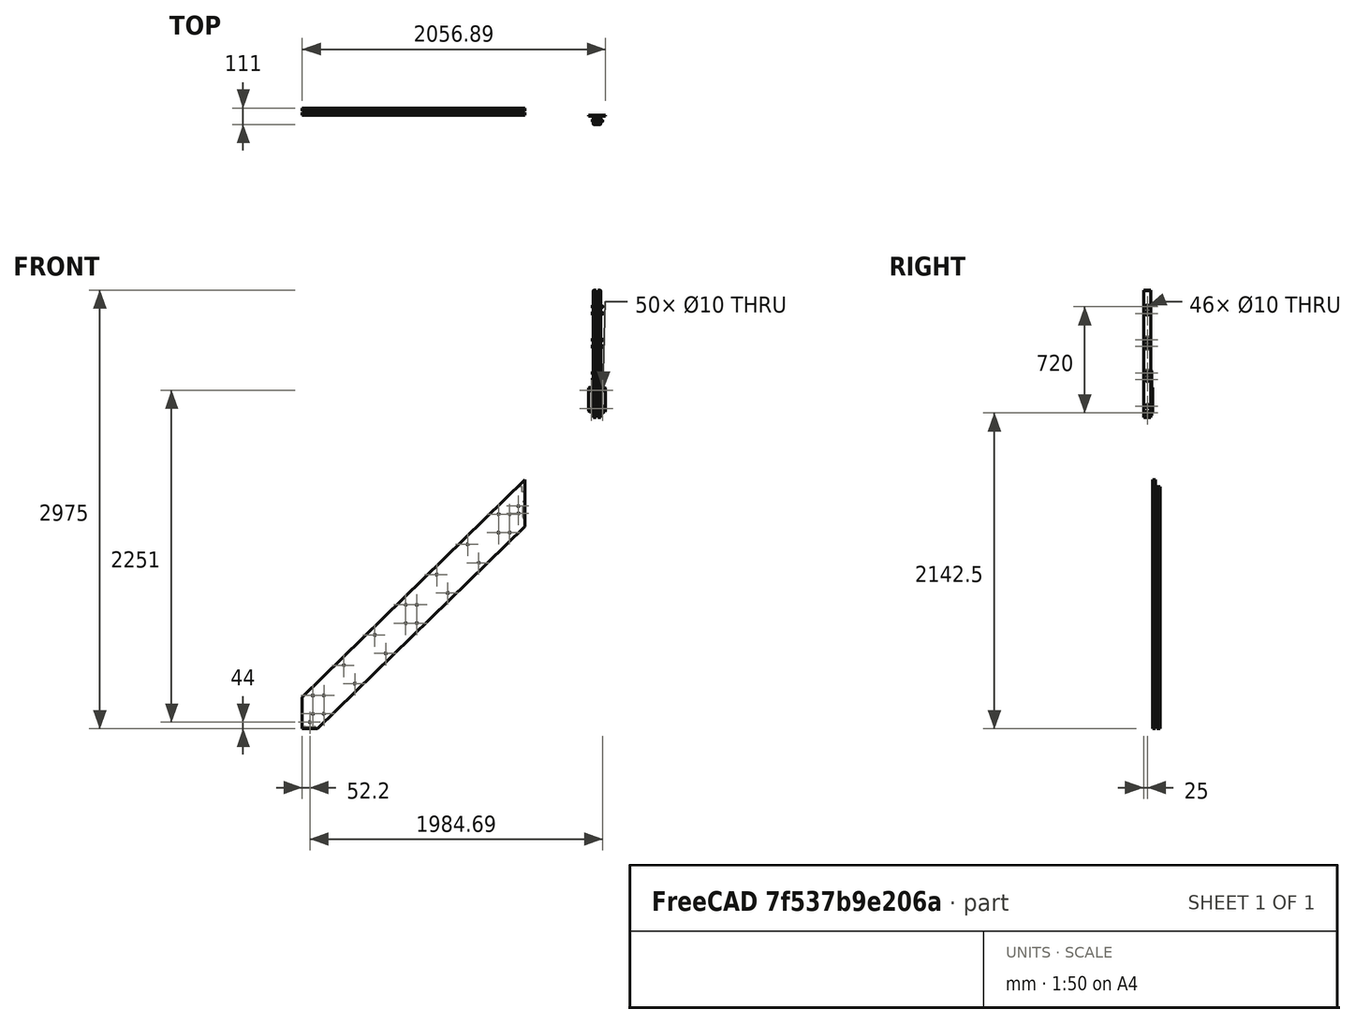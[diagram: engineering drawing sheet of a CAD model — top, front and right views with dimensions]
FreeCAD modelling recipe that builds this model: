
FCSTD DOCUMENT  (FreeCAD 0.17R10993 (Git))
Label: railing_last_wood
License: All rights reserved
LicenseURL: http://en.wikipedia.org/wiki/All_rights_reserved
objects: Part::Part2DObjectPython×22, Part::Feature×5, Part::FeaturePython×3, TechDraw::DrawProjGroupItem×3, App::DocumentObjectGroup×2, Part::Box×1, Part::Mirroring×1, Part::Compound×1, Part::Chamfer×1, Part::Extrusion×1, Part::Cut×1, TechDraw::DrawSVGTemplate×1, TechDraw::DrawProjGroup×1, TechDraw::DrawPage×1
note: 36 computed .brp shape members not serialized (recipe doc carries the construction recipe); baked Part::Feature solids carry a one-line shape summary decoded from their .brp

FEATURE [Part::Box] Box  label="Cube"
  AttacherType = Attacher::AttachEngine3D
  Height = 865
  Length = 20
  Placement = pos=(-25,-23,165) rot=(0,0,1;0rad)
  Width = 50
FEATURE [Part::Mirroring] mirror  label="Mirror of Cube"
  Base = (0,0,0)
  Normal = (1,0,0)
  Source = -> Box
FEATURE [Part::Compound] Compound
  Links = -> [mirror,Box]
  Placement = pos=(89.3902,-413,100) rot=(0,0,1;0rad)
FEATURE [Part::Chamfer] Chamfer  label="railing_wood"
  Base = -> Compound
  Edges = 24 edges r=2: [Edge1,Edge2,Edge3,Edge4,Edge5,Edge6,Edge7,Edge8,Edge9,Edge10,Edge11,Edge12,Edge13,Edge14,Edge15,Edge16,Edge17,Edge18,Edge19,Edge20,Edge21,Edge22,Edge23,Edge24]
FEATURE [Part::Feature] step_01_cs
  shape: bbox 1490 x 3e-07 x 1265 mm, 0 faces, 0 solids (baked)
FEATURE [Part::Feature] fridge_box_panels_01_cs
  shape: bbox 630 x 3e-07 x 2050 mm, 0 faces, 0 solids (baked)
FEATURE [Part::Part2DObjectPython] Line  # Draft 2D object (typed FeaturePython)
  ChamferSize = 0
  Closed = false
  End = (2100,-5,0)
  FilletRadius = 0
  Length = 2100.01
  MakeFace = true
  Points = (2) [(0,0,0),(2100,-5,0)]
  Start = (0,0,0)
  Subdivisions = 0
FEATURE [Part::Part2DObjectPython] Line002  # Draft 2D object (typed FeaturePython)
  ChamferSize = 0
  Closed = false
  End = (2900,0,2260)
  FilletRadius = 0
  Length = 800
  MakeFace = true
  Points = (2) [(2100,0,2260),(2900,0,2260)]
  Start = (2100,0,2260)
  Subdivisions = 0
FEATURE [Part::Part2DObjectPython] DWire  # Draft 2D object (typed FeaturePython)
  ChamferSize = 0
  Closed = false
  End = (2900,0,2105)
  FilletRadius = 0
  Length = 1755
  MakeFace = true
  Points = (4) [(2900,0,2260),(2100,0,2260),(2100,0,2105),(2900,0,2105)]
  Start = (2900,0,2260)
  Subdivisions = 0
FEATURE [Part::Part2DObjectPython] Line003  # Draft 2D object (typed FeaturePython)
  ChamferSize = 0
  Closed = false
  End = (2100,0,3260)
  FilletRadius = 0
  Length = 1000
  MakeFace = true
  Points = (2) [(2100,0,2260),(2100,0,3260)]
  Start = (2100,0,2260)
  Subdivisions = 0
FEATURE [Part::Part2DObjectPython] Line005  # Draft 2D object (typed FeaturePython)
  ChamferSize = 0
  Closed = false
  End = (0,0,1205)
  FilletRadius = 0
  Length = 1000
  MakeFace = true
  Points = (2) [(-1.18132e-16,0,205),(-1.18132e-16,0,1205)]
  Start = (0,0,205)
  Subdivisions = 0
FEATURE [Part::Part2DObjectPython] Line009  # Draft 2D object (typed FeaturePython)
  ChamferSize = 0
  Closed = false
  End = (89.3902,0,1222.39)
  FilletRadius = 0
  Length = 902.176
  MakeFace = true
  Placement = pos=(-630,0,-420.411) rot=(0,0,1;0rad)
  Points = (2) [(719.39,0,740.622),(719.39,0,1642.8)]
  Start = (89.3902,0,320.211)
  Subdivisions = 0
FEATURE [Part::Feature] double_beam_01_cs001
  Placement = pos=(0,365,0) rot=(0,0,1;0rad)
  shape: bbox 1510 x 3e-07 x 1687 mm, 0 faces, 0 solids (baked)
FEATURE [Part::Part2DObjectPython] Line016  # Draft 2D object (typed FeaturePython)
  ChamferSize = 0
  Closed = false
  End = (148.345,-431,590)
  FilletRadius = 0
  Length = 58.9552
  MakeFace = true
  Placement = pos=(2.73e-10,-431,59.7885) rot=(0,0,1;0rad)
  Points = (2) [(89.3902,0,530.211),(148.345,0,530.211)]
  Start = (89.3902,-431,590)
  Subdivisions = 0
FEATURE [Part::Part2DObjectPython] Line019  # Draft 2D object (typed FeaturePython)
  ChamferSize = 0
  Closed = false
  End = (148.345,-431,815)
  FilletRadius = 0
  Length = 58.9552
  MakeFace = true
  Placement = pos=(2.73e-10,-431,284.789) rot=(0,0,1;0rad)
  Points = (2) [(89.3902,0,530.211),(148.345,0,530.211)]
  Start = (89.3902,-431,815)
  Subdivisions = 0
FEATURE [Part::Part2DObjectPython] Line022  # Draft 2D object (typed FeaturePython)
  ChamferSize = 0
  Closed = false
  End = (1490,0,1687.47)
  FilletRadius = 0
  Length = 2110.19
  MakeFace = true
  Points = (2) [(-20,0,213.426),(1490,0,1687.47)]
  Start = (-20,0,213.426)
  Subdivisions = 0
FEATURE [Part::Part2DObjectPython] Line023  # Draft 2D object (typed FeaturePython)
  ChamferSize = 0
  Closed = false
  End = (1490,0,2659.52)
  FilletRadius = 0
  Length = 2110.19
  MakeFace = true
  Placement = pos=(0,0,972.05) rot=(0,0,1;0rad)
  Points = (2) [(-20,0,213.426),(1490,0,1687.47)]
  Start = (-20,0,1185.48)
  Subdivisions = 0
FEATURE [Part::Part2DObjectPython] Line024  # Draft 2D object (typed FeaturePython)
  ChamferSize = 0
  Closed = false
  End = (1524.93,0,2623.75)
  FilletRadius = 0
  Length = 2110.19
  MakeFace = true
  Points = (2) [(14.9268,0,1149.7),(1524.93,0,2623.75)]
  Start = (14.9268,0,1149.7)
  Subdivisions = 0
FEATURE [Part::Part2DObjectPython] Line026  # Draft 2D object (typed FeaturePython)
  ChamferSize = 0
  Closed = false
  End = (148.345,-431,1040)
  FilletRadius = 0
  Length = 58.9552
  MakeFace = true
  Placement = pos=(2.74e-10,-431,509.789) rot=(0,0,1;0rad)
  Points = (2) [(89.3902,0,530.211),(148.345,0,530.211)]
  Start = (89.3902,-431,1040)
  Subdivisions = 0
FEATURE [Part::Part2DObjectPython] Line033  # Draft 2D object (typed FeaturePython)
  ChamferSize = 0
  Closed = false
  End = (89.3902,-431,500)
  FilletRadius = 0
  Length = 58.9552
  MakeFace = true
  Placement = pos=(-58.9552,-431,-30.2115) rot=(0,0,1;0rad)
  Points = (2) [(89.3902,0,530.211),(148.345,0,530.211)]
  Start = (30.4351,-431,500)
  Subdivisions = 0
FEATURE [Part::Part2DObjectPython] Line034  # Draft 2D object (typed FeaturePython)
  ChamferSize = 0
  Closed = false
  End = (89.3902,-431,725)
  FilletRadius = 0
  Length = 58.9552
  MakeFace = true
  Placement = pos=(-58.9552,-431,194.789) rot=(0,0,1;0rad)
  Points = (2) [(89.3902,0,530.211),(148.345,0,530.211)]
  Start = (30.4351,-431,725)
  Subdivisions = 0
FEATURE [Part::Part2DObjectPython] Line035  # Draft 2D object (typed FeaturePython)
  ChamferSize = 0
  Closed = false
  End = (89.3902,-431,950)
  FilletRadius = 0
  Length = 58.9552
  MakeFace = true
  Placement = pos=(-58.9552,-431,419.789) rot=(0,0,1;0rad)
  Points = (2) [(89.3902,0,530.211),(148.345,0,530.211)]
  Start = (30.4351,-431,950)
  Subdivisions = 0
FEATURE [Part::Part2DObjectPython] Line036  # Draft 2D object (typed FeaturePython)
  ChamferSize = 0
  Closed = false
  End = (148.345,-431,365)
  FilletRadius = 0
  Length = 58.9552
  MakeFace = true
  Placement = pos=(2.73e-10,-431,-165.211) rot=(0,0,1;0rad)
  Points = (2) [(89.3902,0,530.211),(148.345,0,530.211)]
  Start = (89.3902,-431,365)
  Subdivisions = 0
FEATURE [Part::Part2DObjectPython] Line037  # Draft 2D object (typed FeaturePython)
  ChamferSize = 0
  Closed = false
  End = (89.3902,-431,275)
  FilletRadius = 0
  Length = 58.9552
  MakeFace = true
  Placement = pos=(-58.9552,-431,-255.211) rot=(0,0,1;0rad)
  Points = (2) [(89.3902,0,530.211),(148.345,0,530.211)]
  Start = (30.4351,-431,275)
  Subdivisions = 0
FEATURE [Part::Part2DObjectPython] Line038  # Draft 2D object (typed FeaturePython)
  ChamferSize = 0
  Closed = false
  End = (89.3902,-431,50)
  FilletRadius = 0
  Length = 58.9552
  MakeFace = true
  Placement = pos=(-58.9552,-431,-480.211) rot=(0,0,1;0rad)
  Points = (2) [(89.3902,0,530.211),(148.345,0,530.211)]
  Start = (30.4351,-431,50)
  Subdivisions = 0
FEATURE [Part::Part2DObjectPython] Line039  # Draft 2D object (typed FeaturePython)
  ChamferSize = 0
  Closed = false
  End = (148.345,-431,140)
  FilletRadius = 0
  Length = 58.9552
  MakeFace = true
  Placement = pos=(2.73e-10,-431,-390.211) rot=(0,0,1;0rad)
  Points = (2) [(89.3902,0,530.211),(148.345,0,530.211)]
  Start = (89.3902,-431,140)
  Subdivisions = 0
FEATURE [Part::Part2DObjectPython] Circle  # Draft 2D object (typed FeaturePython)
  FirstAngle = 0
  LastAngle = 0
  MakeFace = true
  Placement = pos=(64.3902,-411,100) rot=(0.57735,-0.57735,-0.57735;2.0944rad)
  Radius = 5
  Support = -> [Chamfer]
FEATURE [Part::Extrusion] Extrude
  Base = -> Circle
  Dir = (1,0,0)
  DirMode = 0
  FaceMakerClass = Part::FaceMakerBullseye
  LengthFwd = 80
  LengthRev = 0
  Placement = pos=(25,0,0) rot=(0,0,1;0rad)
  Solid = false
  Symmetric = true
FEATURE [Part::FeaturePython] Array  # Draft array (typed FeaturePython)
  Angle = 360
  ArrayType = 0
  Axis = (0,0,1)
  Base = -> Extrude
  Center = (0,0,0)
  Fuse = false
  IntervalAxis = (0,0,0)
  IntervalX = (0,0,45)
  IntervalY = (0,0,225)
  IntervalZ = (0,0,0)
  NumberPolar = 1
  NumberX = 2
  NumberY = 5
  NumberZ = 1
  Placement = pos=(0,0,-27.5) rot=(0,0,1;0rad)
FEATURE [Part::Cut] Cut  label="cutted_railing_wood"
  Base = -> Chamfer
  Placement = pos=(1890,0,1845) rot=(0,0,1;0rad)
  Tool = -> Array
FEATURE [Part::Feature] handrail_01_cs
  shape: bbox 2177 x 1e-05 x 2127 mm, 0 faces, 0 solids (baked)
FEATURE [Part::Feature] Cut_cs
  shape: bbox 50 x 3e-07 x 1100 mm, 0 faces, 0 solids (baked)
FEATURE [Part::Part2DObjectPython] Line043  # Draft 2D object (typed FeaturePython)
  ChamferSize = 0
  Closed = false
  End = (2157.46,-9.99981,3249.6)
  FilletRadius = 0
  Length = 3000
  MakeFace = true
  Points = (2) [(10.7356,-9.99993,1153.99),(2157.46,-9.99981,3249.6)]
  Start = (10.7356,-9.99993,1153.99)
  Subdivisions = 0
FEATURE [Part::Part2DObjectPython] Line044  # Draft 2D object (typed FeaturePython)
  ChamferSize = 0
  Closed = false
  End = (129.39,0,972.5)
  FilletRadius = 0
  Length = 80
  MakeFace = true
  Points = (2) [(49.3902,0,972.5),(129.39,0,972.5)]
  Start = (49.3902,0,972.5)
  Subdivisions = 0
FEATURE [App::DocumentObjectGroup] Group  label="drawing"
  Group = -> [step_01_cs,fridge_box_panels_01_cs,Line,Line002,DWire,Line003,Line005,Line009,double_beam_01_cs001,Line016,Line019,Line022,Line023,Line024,Line026,Line033,Line034,Line035,Line036,Line037,Line038,Line039,Line043,Cut_cs,handrail_01_cs,Line044]
FEATURE [Part::FeaturePython] double_beam_01  # a2plus imported part (geometry in sourceFile) (typed FeaturePython)
  fixedPosition = true
  sourceFile = double_beam.fcstd
  timeLastImport = 1.49424e+09
  updateColors = true
FEATURE [Part::FeaturePython] railing_last_steel_01  # a2plus imported part (geometry in sourceFile) (typed FeaturePython)
  Placement = pos=(1890,0,2070) rot=(0,0,1;0rad)
  fixedPosition = false
  sourceFile = railing_last_steel.fcstd
  timeLastImport = 1.49443e+09
  updateColors = true
FEATURE [App::DocumentObjectGroup] Group001  label="ref"
  Group = -> [double_beam_01,railing_last_steel_01]
FEATURE [TechDraw::DrawSVGTemplate] Template
  Height = 841
  Orientation = 0
  Width = 594
FEATURE [TechDraw::DrawProjGroupItem] ProjItem  label="Front"
  ArcCenterMarks = true
  CenterScale = 2
  Direction = (0,-1,0)
  HardHidden = true
  HiddenWidth = 0.15
  HorizCenterLine = false
  IsoCount = 0
  IsoHidden = false
  IsoVisible = false
  IsoWidth = 0.3
  KeepLabel = false
  LineWidth = 0.1
  Rotation = 0
  RotationVector = (1,0,0)
  Scale = 0.2
  ScaleType = 2
  SeamHidden = false
  SeamVisible = false
  ShowSectionLine = true
  SmoothHidden = false
  SmoothVisible = false
  Source = -> Cut
  Type = 0
  VertCenterLine = false
  X = 0
  Y = 0
FEATURE [TechDraw::DrawProjGroupItem] ProjItem001  label="Left"
  ArcCenterMarks = true
  CenterScale = 2
  Direction = (-1,0,0)
  HardHidden = true
  HiddenWidth = 0.15
  HorizCenterLine = false
  IsoCount = 0
  IsoHidden = false
  IsoVisible = false
  IsoWidth = 0.3
  KeepLabel = false
  LineWidth = 0.1
  Rotation = 0
  RotationVector = (0,1,0)
  Scale = 0.2
  ScaleType = 2
  SeamHidden = false
  SeamVisible = false
  ShowSectionLine = true
  SmoothHidden = false
  SmoothVisible = false
  Source = -> Cut
  Type = 1
  VertCenterLine = false
  X = 35
  Y = 0
FEATURE [TechDraw::DrawProjGroupItem] ProjItem002  label="Top"
  ArcCenterMarks = true
  CenterScale = 2
  Direction = (0,0,1)
  HardHidden = true
  HiddenWidth = 0.15
  HorizCenterLine = false
  IsoCount = 0
  IsoHidden = false
  IsoVisible = false
  IsoWidth = 0.3
  KeepLabel = false
  LineWidth = 0.1
  Rotation = 0
  RotationVector = (1,0,0)
  Scale = 0.2
  ScaleType = 2
  SeamHidden = false
  SeamVisible = false
  ShowSectionLine = true
  SmoothHidden = false
  SmoothVisible = false
  Source = -> Cut
  Type = 4
  VertCenterLine = false
  X = 0
  Y = -123
FEATURE [TechDraw::DrawProjGroup] ProjGroup
  Anchor = -> ProjItem
  AutoDistribute = true
  KeepLabel = false
  ProjectionType = 0
  Rotation = 0
  Scale = 0.2
  ScaleType = 2
  Source = -> Cut
  Views = -> [ProjItem,ProjItem001,ProjItem002]
  X = 297
  Y = 420.5
  spacingX = 25
  spacingY = -50
FEATURE [TechDraw::DrawPage] Page
  ProjectionType = 0
  Template = -> Template
  Views = -> [ProjGroup]
